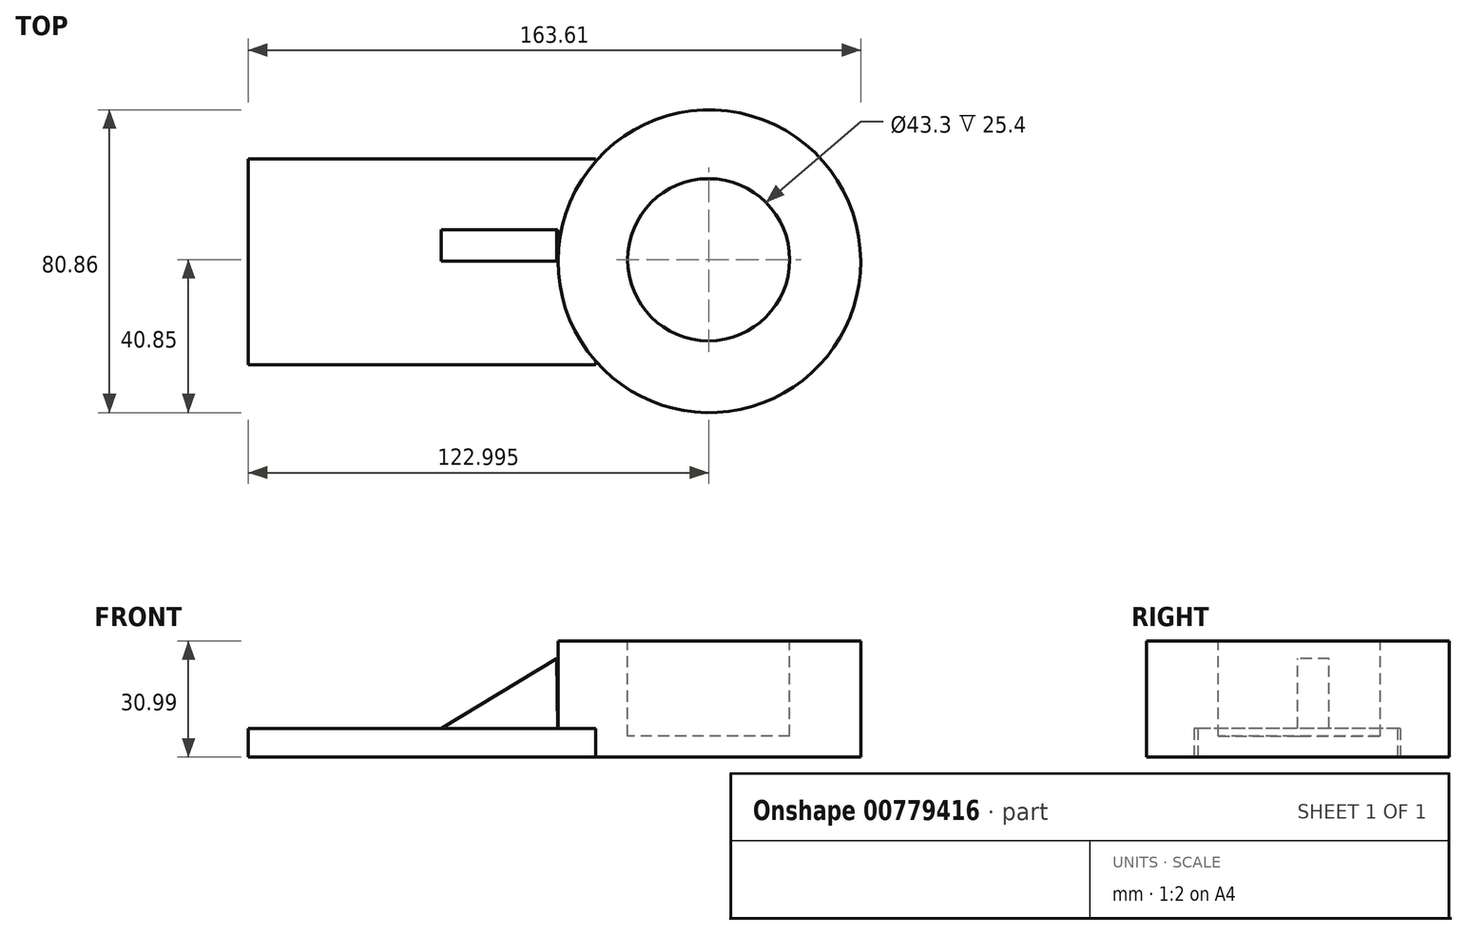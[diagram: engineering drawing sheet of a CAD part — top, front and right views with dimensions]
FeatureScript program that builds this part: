
annotation { "Feature Type Name" : "Feature", "Feature Type Description" : "" }
export const myFeature = defineFeature(function(context is Context, id is Id, definition is map)
    precondition{}
    {
        {
            var Q0;
            Q0=qCreatedBy(makeId("Top.planeOp"),FACE);
            var sketch = newSketch(context, id + "F0", { "sketchPlane" : qUnion([Q0])});
            skCircle(sketch, "E0", {"center": v(47.18, 0) * mm, "radius": 40.43 * mm});
            skSolve(sketch);
        }
        {
            var Q0;
            Q0=makeQuery(id+"F0.imprint","IMPRINT",FACE,{"disambiguationData":[TD([[makeQuery(id+"F0.imprint","IMPRINT",EDGE,{"derivedFrom":sQuery(id+"F0.wireOp",EDGE,"E0")}),1.0]])]});
            extrude(context, id + "F1", {"entities" : qUnion([Q0]), "depth" : 30.99 * mm, "offsetDistance" : 25.4 * mm});
        }
        {
            var Q0;
            Q0=qCreatedBy(makeId("Top.planeOp"),FACE);
            var sketch = newSketch(context, id + "F2", { "sketchPlane" : qUnion([Q0])});
            skLineSegment(sketch, "E1.bottom", {"start": v(-76, 27.38) * mm, "end": v(16.8, 27.38) * mm});
            skLineSegment(sketch, "E1.top", {"start": v(-76, -27.67) * mm, "end": v(16.8, -27.67) * mm});
            skLineSegment(sketch, "E1.left", {"start": v(-76, 27.38) * mm, "end": v(-76, -27.67) * mm});
            skLineSegment(sketch, "E1.right", {"start": v(16.8, 27.38) * mm, "end": v(16.8, -27.67) * mm});
            skSolve(sketch);
        }
        {
            var Q0;
            Q0=makeQuery(id+"F2.imprint","IMPRINT",FACE,{"disambiguationData":[TD([[makeQuery(id+"F2.imprint","IMPRINT",EDGE,{"derivedFrom":sQuery(id+"F2.wireOp",EDGE,"E1.bottom")}),-1.0]])]});
            extrude(context, id + "F3", {"entities" : qUnion([Q0]), "operationType" : NewBodyOperationType.ADD, "depth" : 7.62 * mm, "offsetDistance" : 25.4 * mm});
        }
        {
            var Q0;
            Q0=makeQuery(id+"F1.opExtrude","CAP_FACE",FACE,{"disambiguationData":[OSD([sQuery(id+"F0.wireOp",EDGE,"E0")])],"isStart":false});
            var sketch = newSketch(context, id + "F4", { "sketchPlane" : qUnion([Q0])});
            skCircle(sketch, "E2", {"center": v(47, 0.42) * mm, "radius": 21.65 * mm});
            skSolve(sketch);
        }
        {
            var Q0;
            Q0=makeQuery(id+"F4.imprint","IMPRINT",FACE,{"disambiguationData":[TD([[makeQuery(id+"F4.imprint","IMPRINT",EDGE,{"derivedFrom":sQuery(id+"F4.wireOp",EDGE,"E2")}),1.0]])]});
            extrude(context, id + "F5", {"entities" : qUnion([Q0]), "operationType" : NewBodyOperationType.REMOVE, "oppositeDirection" : true, "depth" : 25.4 * mm, "offsetDistance" : 25.4 * mm});
        }
        {
            var Q0;
            Q0=qCreatedBy(makeId("Front.planeOp"),FACE);
            var sketch = newSketch(context, id + "F6", { "sketchPlane" : qUnion([Q0])});
            skLineSegment(sketch, "E3", {"start": v(6.42, 26.34) * mm, "end": v(-24.46, 7.65) * mm});
            skLineSegment(sketch, "E4", {"start": v(-24.46, 7.65) * mm, "end": v(6.7, 7.65) * mm});
            skLineSegment(sketch, "E5", {"start": v(6.7, 7.65) * mm, "end": v(6.42, 26.34) * mm});
            skSolve(sketch);
        }
        {
            var Q0;
            Q0=makeQuery(id+"F6.imprint","IMPRINT",FACE,{"disambiguationData":[TD([[makeQuery(id+"F6.imprint","IMPRINT",EDGE,{"derivedFrom":sQuery(id+"F6.wireOp",EDGE,"E3")}),1.0]])]});
            extrude(context, id + "F7", {"entities" : qUnion([Q0]), "oppositeDirection" : true, "depth" : 8.38 * mm, "offsetDistance" : 25.4 * mm});
        }
    });
